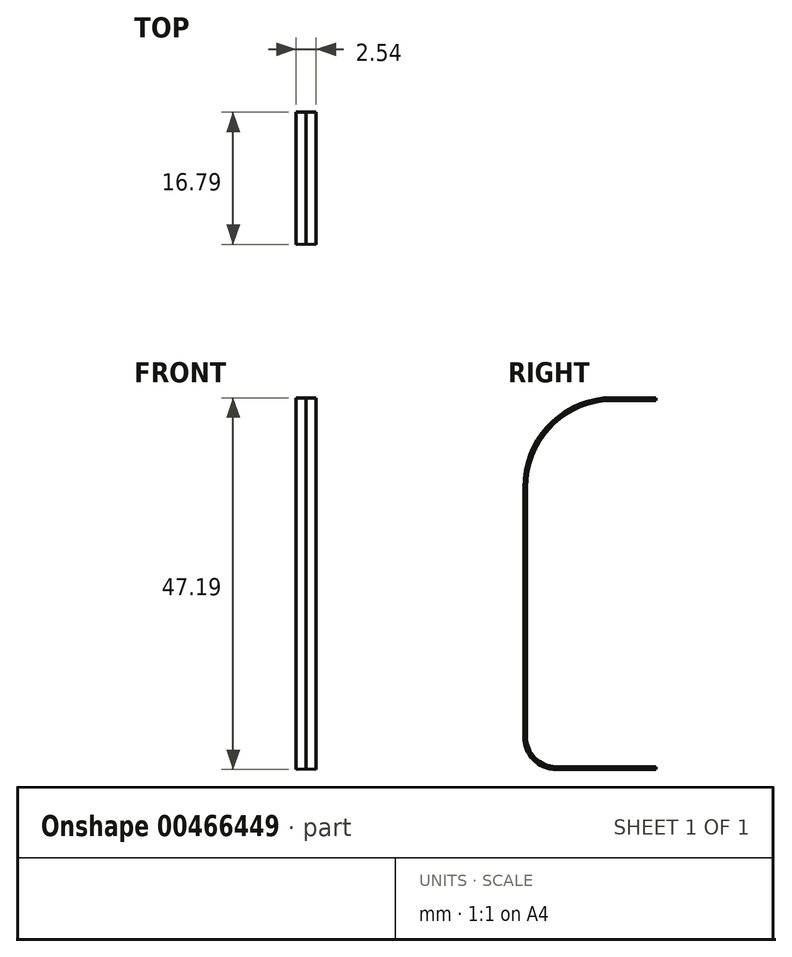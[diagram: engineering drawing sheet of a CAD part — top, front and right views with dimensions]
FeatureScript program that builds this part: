
annotation { "Feature Type Name" : "Feature", "Feature Type Description" : "" }
export const myFeature = defineFeature(function(context is Context, id is Id, definition is map)
    precondition{}
    {
        {
            var Q0;
            Q0=qCreatedBy(makeId("Right.planeOp"),FACE);
            var sketch = newSketch(context, id + "F0", { "sketchPlane" : qUnion([Q0])});
            skLineSegment(sketch, "E0", {"start": v(0, 0) * mm, "end": v(-12.7, 0) * mm});
            skLineSegment(sketch, "E1", {"start": v(-16.79, 4.09) * mm, "end": v(-16.79, 35.84) * mm});
            skLineSegment(sketch, "E2", {"start": v(-6.35, 47.2) * mm, "end": v(0, 47.2) * mm});
            skArc(sketch, "E3", {"start": v(-6.65, 47.17) * mm, "mid": v(-13.89, 43.44) * mm, "end": v(-16.79, 35.84) * mm});
            skPoint(sketch, "E4.visualSharp", {"position": v(-6.5, 47.2) * mm});
            skArc(sketch, "E4.filletArc", {"start": v(-6.35, 47.2) * mm, "mid": v(-6.5, 47.19) * mm, "end": v(-6.65, 47.17) * mm});
            skArc(sketch, "E5", {"start": v(-16.79, 4.09) * mm, "mid": v(-15.6, 1.2) * mm, "end": v(-12.7, 0) * mm});
            skSolve(sketch);
        }
        {
            var Q0;
            Q0=qCreatedBy(makeId("Front.planeOp"),FACE);
            var sketch = newSketch(context, id + "F1", { "sketchPlane" : qUnion([Q0])});
            skLineSegment(sketch, "E6.top", {"start": v(-1.27, 0.34) * mm, "end": v(1.27, 0.34) * mm});
            skLineSegment(sketch, "E6.left", {"start": v(-1.27, 0) * mm, "end": v(-1.27, 0.34) * mm});
            skLineSegment(sketch, "E6.right", {"start": v(1.27, 0) * mm, "end": v(1.27, 0.34) * mm});
            skLineSegment(sketch, "E7", {"start": v(0, 0.34) * mm, "end": v(0, 0) * mm});
            skLineSegment(sketch, "E8", {"start": v(0, 0.04) * mm, "end": v(1.27, 0) * mm});
            skLineSegment(sketch, "E9", {"start": v(0, 0.04) * mm, "end": v(-1.27, 0) * mm});
            skSolve(sketch);
        }
        {
            var Q0;
            {var subQ0=sQuery(id+"F1.wireOp",EDGE,"E6.right");Q0=makeQuery(id+"F1.imprint","IMPRINT",FACE,{"disambiguationData":[TD([[makeQuery(id+"F1.imprint","IMPRINT",EDGE,{"derivedFrom":subQ0}),1.0]])]});}
            var Q1;
            {var subQ0=sQuery(id+"F1.wireOp",EDGE,"E6.left");Q1=makeQuery(id+"F1.imprint","IMPRINT",FACE,{"disambiguationData":[TD([[makeQuery(id+"F1.imprint","IMPRINT",EDGE,{"derivedFrom":subQ0}),-1.0]])]});}
            var Q2;
            Q2=sQuery(id+"F0.wireOp",EDGE,"E0");
            var Q3;
            Q3=sQuery(id+"F0.wireOp",EDGE,"E5");
            var Q4;
            Q4=sQuery(id+"F0.wireOp",EDGE,"E1");
            var Q5;
            Q5=sQuery(id+"F0.wireOp",EDGE,"E3");
            var Q6;
            Q6=sQuery(id+"F0.wireOp",EDGE,"E2");
            var Q7;
            Q7=sQuery(id+"F0.wireOp",EDGE,"E4.filletArc");
            sweep(context, id + "F2", {"profiles" : qUnion([Q0, Q1]), "path" : qUnion([Q2, Q3, Q4, Q5, Q6, Q7])});
        }
    });
